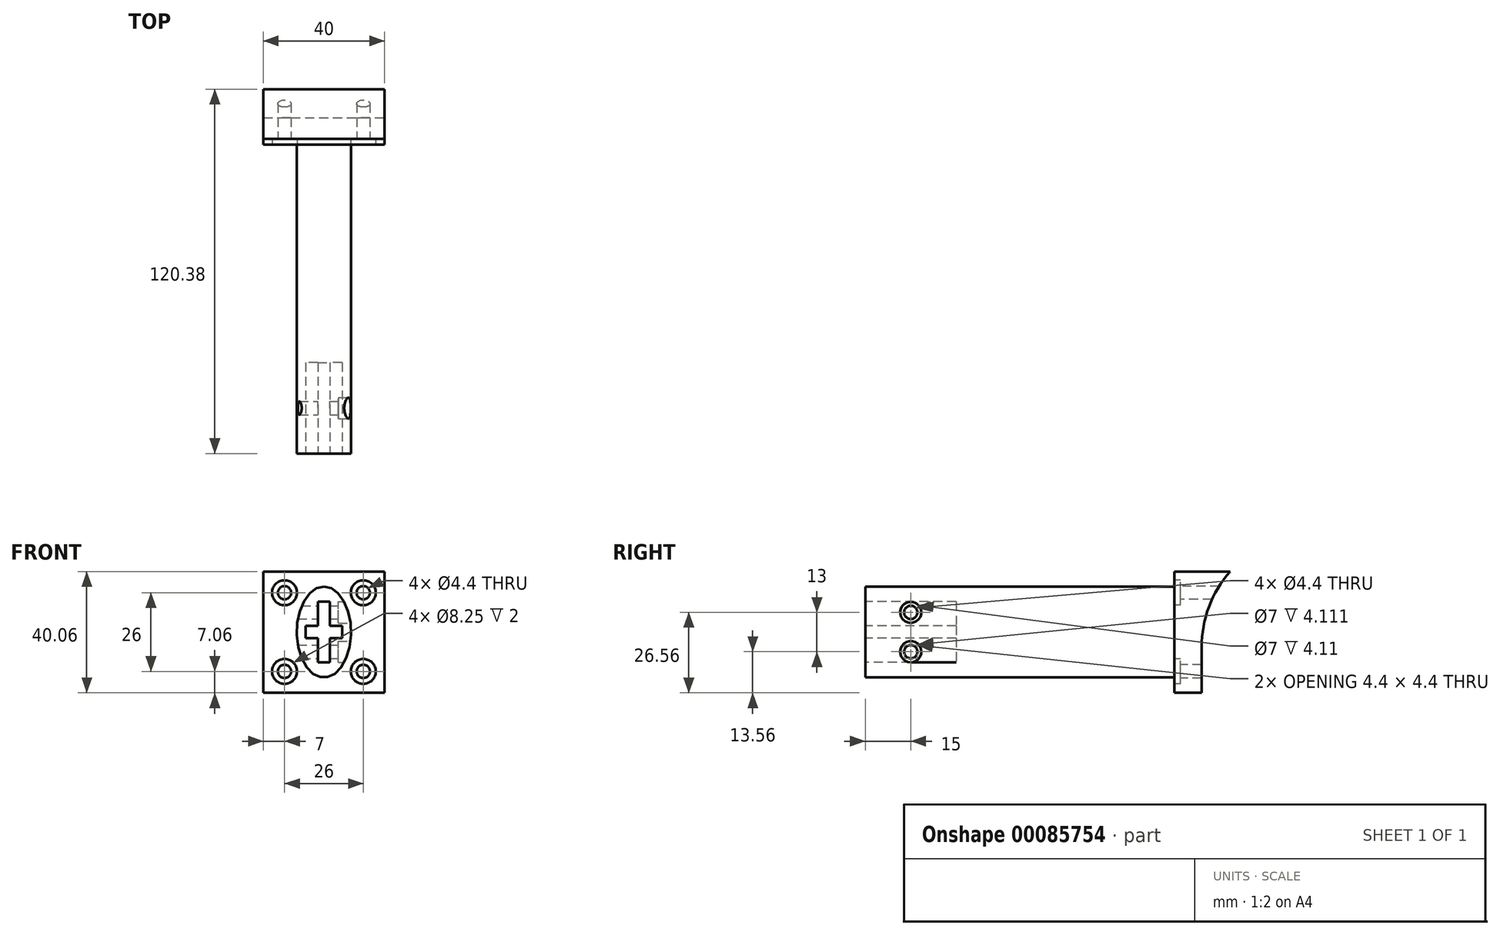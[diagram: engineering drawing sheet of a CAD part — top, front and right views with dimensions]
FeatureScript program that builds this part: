
annotation { "Feature Type Name" : "Feature", "Feature Type Description" : "" }
export const myFeature = defineFeature(function(context is Context, id is Id, definition is map)
    precondition{}
    {
        {
            var Q0;
            Q0=qCreatedBy(makeId("Front.planeOp"),FACE);
            var sketch = newSketch(context, id + "F0", { "sketchPlane" : qUnion([Q0])});
            skLineSegment(sketch, "E0.bottom", {"start": v(20, -20) * mm, "end": v(-20, -20) * mm});
            skLineSegment(sketch, "E0.top", {"start": v(20, 20) * mm, "end": v(-20, 20) * mm});
            skLineSegment(sketch, "E0.left", {"start": v(20, -20) * mm, "end": v(20, 20) * mm});
            skLineSegment(sketch, "E0.right", {"start": v(-20, -20) * mm, "end": v(-20, 20) * mm});
            skSolve(sketch);
        }
        {
            var Q0;
            Q0=makeQuery(id+"F0.imprint","IMPRINT",FACE,{"disambiguationData":[TD([[makeQuery(id+"F0.imprint","IMPRINT",EDGE,{"derivedFrom":sQuery(id+"F0.wireOp",EDGE,"E0.bottom")}),-1.0]])]});
            var sketch = newSketch(context, id + "F1", { "sketchPlane" : qUnion([Q0])});
            skEllipse(sketch, "E1", {"center": v(0, 0) * mm, "majorRadius": 15 * mm, "minorRadius": 9 * mm, "majorAxis": v(0, 1)});
            skPoint(sketch, "E2", {"position": v(-9, 0) * mm});
            skPoint(sketch, "E3", {"position": v(0, 15) * mm});
            skPoint(sketch, "E4", {"position": v(9, 0) * mm});
            skSolve(sketch);
        }
        {
            var Q0;
            Q0=qCreatedBy(makeId("Front.planeOp"),FACE);
            var sketch = newSketch(context, id + "F2", { "sketchPlane" : qUnion([Q0])});
            skPoint(sketch, "E5.center.orphan", {"position": v(-13, 13) * mm});
            skPoint(sketch, "E6.MirrorP", {"position": v(13, 13) * mm});
            skPoint(sketch, "E7.MirrorP", {"position": v(-13, -13) * mm});
            skPoint(sketch, "E8.MirrorP", {"position": v(13, -13) * mm});
            skSolve(sketch);
        }
        {
            var Q0;
            Q0 = qSketchRegion(id + "F0", true);
            extrude(context, id + "F3", {"entities" : qUnion([Q0]), "oppositeDirection" : true, "depth" : 4 * mm});
        }
        {
            var Q0;
            Q0 = qSketchRegion(id + "F1", true);
            extrude(context, id + "F4", {"entities" : qUnion([Q0]), "operationType" : NewBodyOperationType.ADD, "depth" : 50 * mm});
        }
        {
            var Q0;
            Q0=makeQuery(id+"F4.opExtrude","CAP_FACE",FACE,{"disambiguationData":[OSD([sQuery(id+"F1.wireOp",EDGE,"E1")])],"isStart":false});
            extrude(context, id + "F5", {"entities" : qUnion([Q0]), "operationType" : NewBodyOperationType.ADD, "depth" : 50 * mm});
        }
        {
            var Q0;
            Q0=qCreatedBy(makeId("Right.planeOp"),FACE);
            var sketch = newSketch(context, id + "F6", { "sketchPlane" : qUnion([Q0])});
            skArc(sketch, "E9", {"start": v(20.38, 19.94) * mm, "mid": v(13.43, 8.33) * mm, "end": v(11, -4.97) * mm});
            skLineSegment(sketch, "E10.top", {"start": v(4, -20.06) * mm, "end": v(11, -20.06) * mm});
            skLineSegment(sketch, "E10.left", {"start": v(4, 19.94) * mm, "end": v(4, -20.06) * mm});
            skPoint(sketch, "E11", {"position": v(20.38, 19.94) * mm});
            skLineSegment(sketch, "E12", {"start": v(20.38, 19.94) * mm, "end": v(4, 19.94) * mm});
            skLineSegment(sketch, "E13", {"start": v(11, -4.97) * mm, "end": v(11, -20.06) * mm});
            skLineSegment(sketch, "E14", {"start": v(11, -4.97) * mm, "end": v(11, -4.97) * mm});
            skPoint(sketch, "E15.orphan", {"position": v(11, -5.06) * mm});
            skPoint(sketch, "E16.end.orphan", {"position": v(11, 43.1) * mm});
            skSolve(sketch);
        }
        {
            var Q0;
            Q0=makeQuery(id+"F6.imprint","IMPRINT",FACE,{"disambiguationData":[TD([[makeQuery(id+"F6.imprint","IMPRINT",EDGE,{"derivedFrom":sQuery(id+"F6.wireOp",EDGE,"E9")}),-1.0]])]});
            extrude(context, id + "F7", {"entities" : qUnion([Q0]), "operationType" : NewBodyOperationType.ADD, "endBound" : BoundingType.SYMMETRIC, "oppositeDirection" : true, "depth" : 40 * mm});
        }
        {
            var Q0;
            Q0=makeQuery(id+"F3.opExtrude","CAP_FACE",FACE,{"disambiguationData":[OSD([sQuery(id+"F0.wireOp",EDGE,"E0.bottom"),sQuery(id+"F0.wireOp",EDGE,"E0.top"),sQuery(id+"F0.wireOp",EDGE,"E0.left"),sQuery(id+"F0.wireOp",EDGE,"E0.right")])],"isStart":true});
            extrude(context, id + "F8", {"entities" : qUnion([Q0]), "operationType" : NewBodyOperationType.REMOVE, "oppositeDirection" : true, "depth" : 2 * mm});
        }
        {
            var Q0;
            Q0=sQuery(id+"F2.wireOp",VERTEX,"E5.center.orphan");
            var Q1;
            Q1=sQuery(id+"F2.wireOp",VERTEX,"E6.MirrorP");
            var Q2;
            Q2=sQuery(id+"F2.wireOp",VERTEX,"E8.MirrorP");
            var Q3;
            Q3=sQuery(id+"F2.wireOp",VERTEX,"E7.MirrorP");
            var Q4;
            Q4=makeQuery(id+"F3.opExtrude","SWEPT_BODY",BODY,{"disambiguationData":[OSD([sQuery(id+"F0.wireOp",EDGE,"E0.bottom"),sQuery(id+"F0.wireOp",EDGE,"E0.top"),sQuery(id+"F0.wireOp",EDGE,"E0.left"),sQuery(id+"F0.wireOp",EDGE,"E0.right")])]});
            var Q5;
            Q5=makeQuery(id+"F7.split0.splitOp","SPLIT",BODY,{"derivedFrom":makeQuery(id+"F7.opExtrude","SWEPT_BODY",BODY,{"disambiguationData":[OSD([sQuery(id+"F6.wireOp",EDGE,"E9"),sQuery(id+"F6.wireOp",EDGE,"E10.top"),sQuery(id+"F6.wireOp",EDGE,"E10.left"),sQuery(id+"F6.wireOp",EDGE,"E12"),sQuery(id+"F6.wireOp",EDGE,"E13")])]})});
            hole(context, id + "F9", {"style" : HoleStyle.C_BORE, "endStyle" : HoleEndStyle.BLIND, "standardTappedOrClearance" : lookupTablePath({ "standard" : "ISO", "fit" : "Normal", "size" : "M4", "type" : "Clearance" }), "standardBlindInLast" : lookupTablePath({ "fit" : "Standard", "standard" : "ISO", "size" : "M4", "type" : "Clearance" }), "holeDiameter" : 4.4 * mm, "cBoreDiameter" : 8.25 * mm, "cBoreDepth" : 4 * mm, "holeDepth" : 50 * mm, "startFromSketch" : true, "locations" : qUnion([Q0, Q1, Q2, Q3]), "scope" : qUnion([Q4, Q5])});
        }
        {
            var Q0;
            Q0=qCreatedBy(makeId("Right.planeOp"),FACE);
            cPlane(context, id + "F10", {"entities" : qUnion([Q0]), "cplaneType" : CPlaneType.OFFSET, "offset" : 14 * mm, "width" : 150 * mm, "height" : 150 * mm});
        }
        {
            var Q0;
            Q0=qCreatedBy(id+"F10.planeOp",FACE);
            var sketch = newSketch(context, id + "F11", { "sketchPlane" : qUnion([Q0])});
            skPoint(sketch, "E17", {"position": v(-85, 6.5) * mm});
            skPoint(sketch, "E18.MirrorP", {"position": v(-85, -6.5) * mm});
            skSolve(sketch);
        }
        {
            var Q0;
            Q0=sQuery(id+"F11.wireOp",VERTEX,"E17");
            var Q1;
            Q1=sQuery(id+"F11.wireOp",VERTEX,"E18.MirrorP");
            var Q2;
            Q2=makeQuery(id+"F3.opExtrude","SWEPT_BODY",BODY,{"disambiguationData":[OSD([sQuery(id+"F0.wireOp",EDGE,"E0.bottom"),sQuery(id+"F0.wireOp",EDGE,"E0.top"),sQuery(id+"F0.wireOp",EDGE,"E0.left"),sQuery(id+"F0.wireOp",EDGE,"E0.right")])]});
            hole(context, id + "F12", {"style" : HoleStyle.C_BORE, "endStyle" : HoleEndStyle.BLIND, "holeDiameter" : 4.4 * mm, "cBoreDiameter" : 7 * mm, "cBoreDepth" : 2 * mm, "holeDepth" : 30 * mm, "locations" : qUnion([Q0, Q1]), "scope" : qUnion([Q2])});
        }
        {
            var Q0;
            Q0=makeQuery(id+"F5.opExtrude","CAP_FACE",FACE,{"disambiguationData":[OSD([sQuery(id+"F1.wireOp",EDGE,"E1")])],"isStart":false});
            var sketch = newSketch(context, id + "F13", { "sketchPlane" : qUnion([Q0])});
            skLineSegment(sketch, "E19", {"start": v(0, 10) * mm, "end": v(2, 10) * mm});
            skLineSegment(sketch, "E20", {"start": v(2, 10) * mm, "end": v(2, 2) * mm});
            skLineSegment(sketch, "E21", {"start": v(2, 2) * mm, "end": v(6, 2) * mm});
            skLineSegment(sketch, "E22", {"start": v(6, 2) * mm, "end": v(6, -2) * mm});
            skLineSegment(sketch, "E23", {"start": v(6, -2) * mm, "end": v(2, -2) * mm});
            skLineSegment(sketch, "E24", {"start": v(2, -2) * mm, "end": v(2, -10) * mm});
            skLineSegment(sketch, "E25", {"start": v(2, -10) * mm, "end": v(0, -10) * mm});
            skLineSegment(sketch, "E26", {"start": v(0, 10) * mm, "end": v(-2, 10) * mm});
            skLineSegment(sketch, "E27", {"start": v(-2, 10) * mm, "end": v(-2, 2) * mm});
            skLineSegment(sketch, "E28", {"start": v(-2, 2) * mm, "end": v(-6, 2) * mm});
            skLineSegment(sketch, "E29", {"start": v(-6, 2) * mm, "end": v(-6, -2) * mm});
            skLineSegment(sketch, "E30", {"start": v(-6, -2) * mm, "end": v(-2, -2) * mm});
            skLineSegment(sketch, "E31", {"start": v(-2, -2) * mm, "end": v(-2, -10) * mm});
            skLineSegment(sketch, "E32", {"start": v(-2, -10) * mm, "end": v(0, -10) * mm});
            skSolve(sketch);
        }
        {
            var Q0;
            Q0=makeQuery(id+"F13.imprint","IMPRINT",FACE,{"disambiguationData":[TD([[makeQuery(id+"F13.imprint","IMPRINT",EDGE,{"derivedFrom":sQuery(id+"F13.wireOp",EDGE,"E19")}),-1.0]])]});
            extrude(context, id + "F14", {"entities" : qUnion([Q0]), "operationType" : NewBodyOperationType.REMOVE, "oppositeDirection" : true, "depth" : 30 * mm});
        }
    });
